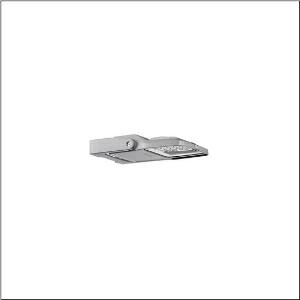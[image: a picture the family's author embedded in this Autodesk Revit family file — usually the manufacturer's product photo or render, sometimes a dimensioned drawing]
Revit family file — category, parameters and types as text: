
# Revit family: floodlight_fl_21_iq_micro___pl52_5xa7761a2d2a_1372
name_source: partatom
category: Lighting Fixtures
units: mm (PartAtom-declared; Revit-internal decimal feet)

## family parameters
Cut with Voids When Loaded = No
Host = Face
Light Source = No
Part Type = Normal
Room Calculation Point = No
Round Connector Dimension = Use Diameter
Shared = No

## types (1)
- --- (1 x LED, 2890 lm, 23.1 W, 3000K)
    Apparent Load = 23 VA
    CIE Flux Codes = 26 60 98 100 100
    Color Rendering = 70
    Color Temperature = 3000K
    Default Elevation = 1800 mm
    Description = Floodlight FL 21 iQ micro, floodlight, primary light control with lens, of PMMA, primary optical cover: protective disc, of toughened safety glass, transparent, light distribution: PL52, light emission: direct distribution, installation type: surface-mounted, LED, High Power LED, rated luminous flux: 2.890lm, luminous efficacy: 125lm/W, light colour: 730, colour temperature: 3000K, control: optimised constant luminous flux control (CLO 2.0), Desk-Remote (wireless, voltage-free reading and setting of iQ features in the workshop via application-optimized NFC function/RFID function), Light-Fading, Smart-Wire, Night-Set, Lumen-Switch, Temp-Guard, Auto-Match, with terminal, 6-pole, mains connection: 220..240V, AC, 50/60Hz, start of lifetime: 23W, end of service life: 24W, reduction: 11W, luminaire housing, of diecast aluminium, powder-coated, Siteco® metallic grey (DB 702S), corrosivity category C5 mid according to DIN EN ISO 12944, sealing non-destructively replaceable, design bracket, of diecast aluminium, powder-coated, Siteco® metallic grey (DB 702S), protection rating (complete): IP66, insulation class (complete): insulation class II (safety insulation), certification: CE, ENEC, VDE, protection symbol: D, impact resistance: IK07, permissible operating ambient temperature: -40..+40°C, permissible operating ambient temperature for outdoor applications: -40..+50°C, standard: DIN EN 12944, LABS conformity tested according to VDMA 24364:2018-05, packaging unit: 1 piece

Light Distribution: PL52
    Height = 65 mm
    Lamp = 1 x LED
    Lamp Light Flux = 2890 lm
    Lamp Power = 23.1 W
    Lamp count = 1
    Length = 312 mm
    Luminous efficacy = 125 lm/W
    Manufacturer = Siteco
    ModVariant = No
    Model = 5XA7761A2D2A
    Mounting Place = Wall
    Mounting Type = Surface mounted
    Number of Poles = 1
    OnlyDefault = Yes
    Power Factor = 1
    Product Name = Floodlight FL 21 iQ micro | PL52
    Product group = floodlight | wall mounted
    ProductGroupID = 2001
    Protection Class = Protection class II
    Protection Degree = IP 66
    RLX_Detail_Level = 1
    RLX_Emergency_Light_Flux = 0 lm
    RLX_Emergency_Type = 0
    RLX_Emergency_Type_DB = No
    RlxData = <blob elided: 97625 chars, md5=9e3bc325>
    Socket = socket
    Standby Power = 0 W
    System Light Flux = 2890 lm
    System Power = 23 W
    Type Comments = factory setting: luminous flux: 100 % | dim-lin: 254 | 455 mA
    Type Image = l_1006878.jpg
    URL = http://relux.com
    VarID = @adj_149419
    Voltage = 0 V
    Weight = 0.00 kg
    Width = 230 mm

## geometry (parser evidence)
native form markers: Blend x4, Sweep x14
no freeform markers — native parametric forms only
